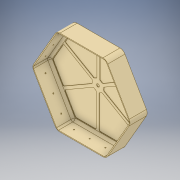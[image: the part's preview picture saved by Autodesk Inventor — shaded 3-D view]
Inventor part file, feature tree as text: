
AUTODESK INVENTOR PART (.ipt)
format: ipt  version: 2019 (Build 230136000, 136)  size: 318,464 bytes
history: native  units: mm
features: mirror x4, extrude x3, sketch x3, plane x3, fillet x3, projected_geometry x2, shell x1
ambient origin geometry x8: Origin, YZ Plane, XZ Plane, XY Plane, X Axis, Y Axis, Z Axis, Center Point
bodies: Solid1 (feature_tree)
feature tree (19):
  extrude  "Extrusion1"  Depth=30.0mm TaperAngle=0.0deg
  shell  "Shell1"  Thickness=1.5mm
  sketch  "Sketch2"  dims[d5=2.0mm d6=15.0mm]
  plane  "Work Plane1"
  plane  "Work Plane2"
  plane  "Work Plane3"
  extrude  "Extrusion5"  Depth=2.0mm
  extrude  "Extrusion2"  Depth=1.0mm TaperAngle=0.0deg
  mirror  "Mirror1"
  mirror  "Mirror2"
  mirror  "Mirror3"
  mirror  "Mirror4"
  fillet  "Fillet1"  Radius=4.0mm
  fillet  "Fillet2"  Radius=10.0mm
  fillet  "Fillet4"  Radius=1.0mm
  sketch  "Sketch1"  dims[d0=150.0mm d2=30.0mm d3=0.0mm d4=1.5mm]
  projected_geometry  "Projected Loop1"
  sketch  "Sketch4"  dims[d7=15.0mm d8=1.0mm d9=0.0mm d10=4.0mm d11=10.0mm d12=1.0mm d37=5.0mm d44=10.0mm d45=60.0deg d46=90.0deg d47=90.0deg d48=60.0mm d50=360.0deg d52=5.5mm d53=0.75mm d54=0.0mm d55=5.0mm d56=2.0mm]
  projected_geometry  "Projected Loop3"
